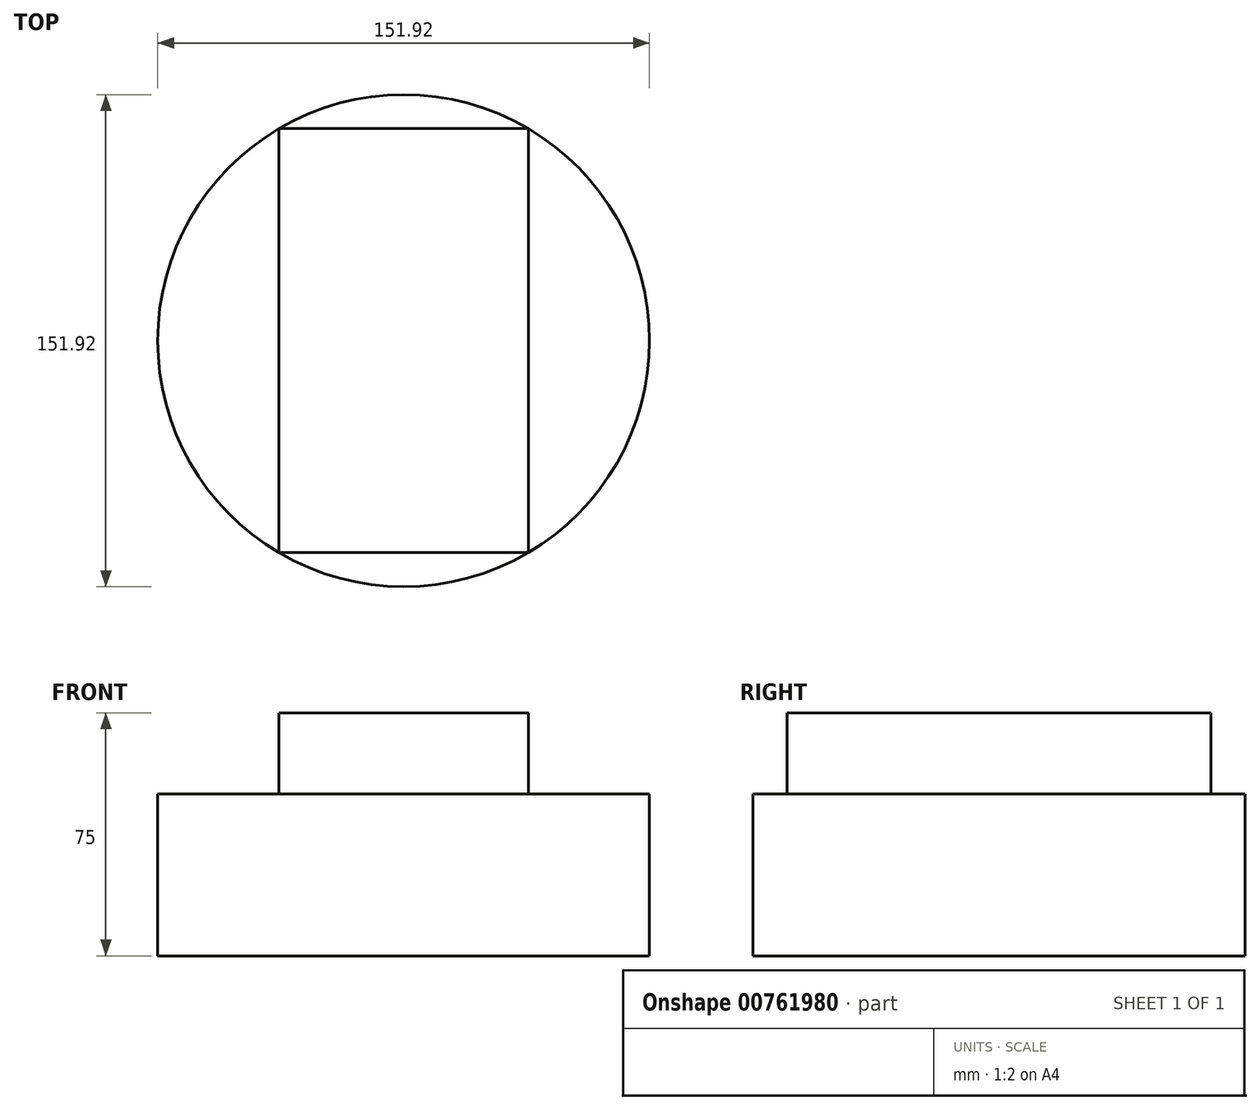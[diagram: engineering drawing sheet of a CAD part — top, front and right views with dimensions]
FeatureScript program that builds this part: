
annotation { "Feature Type Name" : "Feature", "Feature Type Description" : "" }
export const myFeature = defineFeature(function(context is Context, id is Id, definition is map)
    precondition{}
    {
        {
            var Q0;
            Q0=qCreatedBy(makeId("Top.planeOp"),FACE);
            var sketch = newSketch(context, id + "F0", { "sketchPlane" : qUnion([Q0])});
            skCircle(sketch, "E0", {"center": v(0, 0) * mm, "radius": 75.96 * mm});
            skSolve(sketch);
        }
        {
            var Q0;
            Q0=makeQuery(id+"F0.imprint","IMPRINT",FACE,{"disambiguationData":[TD([[makeQuery(id+"F0.imprint","IMPRINT",EDGE,{"derivedFrom":sQuery(id+"F0.wireOp",EDGE,"E0")}),1.0]])]});
            var Q1;
            Q1=sQuery(id+"F0.wireOp",EDGE,"E0");
            extrude(context, id + "F1", {"entities" : qUnion([Q0]), "surfaceEntities" : qUnion([Q1]), "depth" : 50 * mm, "offsetDistance" : 25.4 * mm});
        }
        {
            var Q0;
            Q0=makeQuery(id+"F1.opExtrude","CAP_FACE",FACE,{"disambiguationData":[OSD([sQuery(id+"F0.wireOp",EDGE,"E0")])],"isStart":false});
            var sketch = newSketch(context, id + "F2", { "sketchPlane" : qUnion([Q0])});
            skLineSegment(sketch, "E1.bottom", {"start": v(38.53, 65.46) * mm, "end": v(-38.53, 65.46) * mm});
            skLineSegment(sketch, "E1.top", {"start": v(38.53, -65.46) * mm, "end": v(-38.53, -65.46) * mm});
            skLineSegment(sketch, "E1.left", {"start": v(38.53, 65.46) * mm, "end": v(38.53, -65.46) * mm});
            skLineSegment(sketch, "E1.right", {"start": v(-38.53, 65.46) * mm, "end": v(-38.53, -65.46) * mm});
            skPoint(sketch, "E1.middle", {"position": v(0, 0) * mm});
            skSolve(sketch);
        }
        {
            var Q0;
            Q0 = qSketchRegion(id + "F2", true);
            extrude(context, id + "F3", {"entities" : qUnion([Q0]), "operationType" : NewBodyOperationType.ADD, "depth" : 25 * mm, "offsetDistance" : 25.4 * mm});
        }
    });
